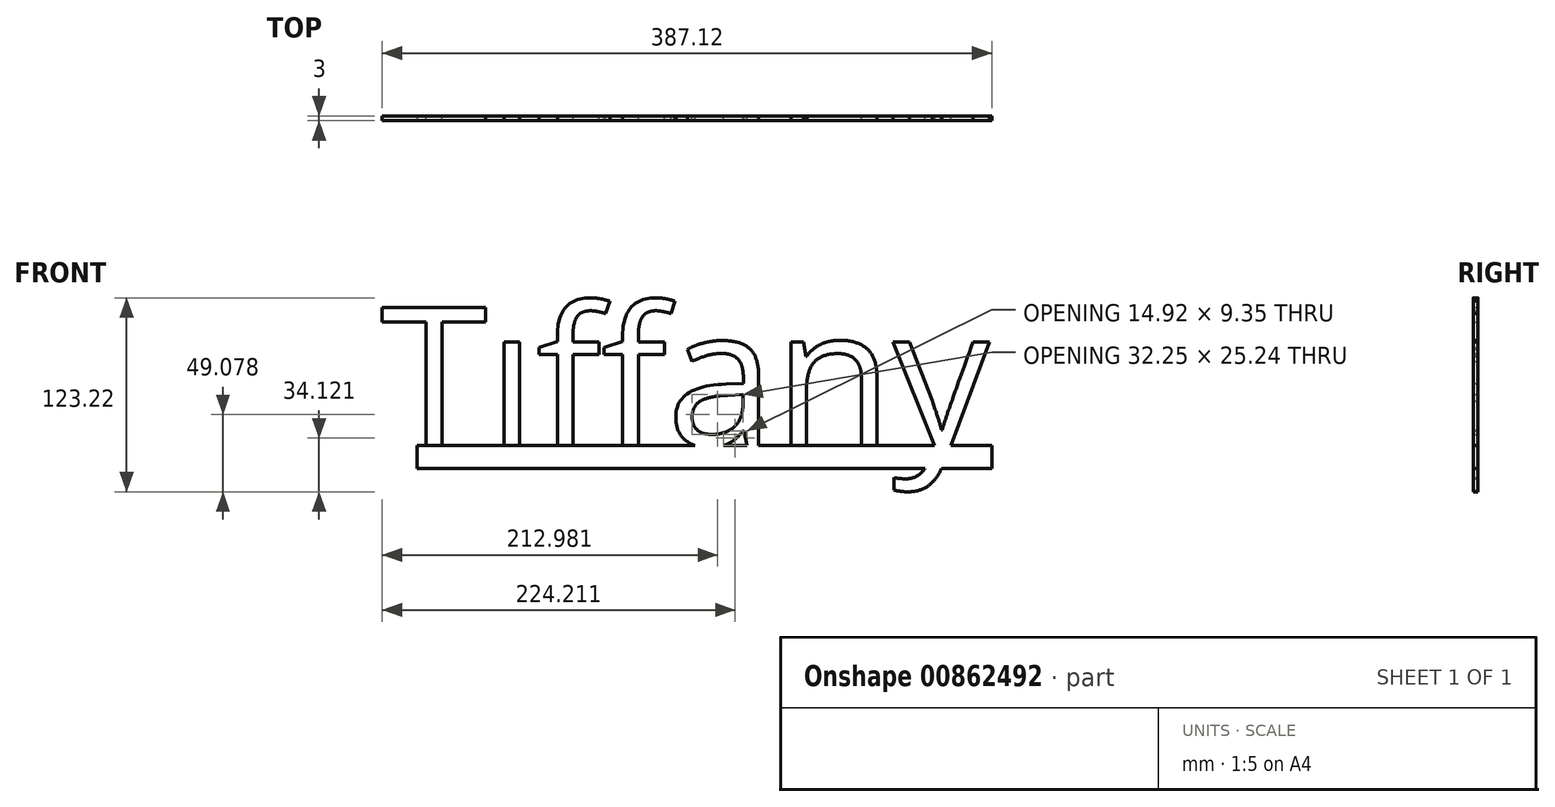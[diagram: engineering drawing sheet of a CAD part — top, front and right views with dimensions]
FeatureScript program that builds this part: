
annotation { "Feature Type Name" : "Feature", "Feature Type Description" : "" }
export const myFeature = defineFeature(function(context is Context, id is Id, definition is map)
    precondition{}
    {
        {
            var Q0;
            Q0=qCreatedBy(makeId("Front.planeOp"),FACE);
            var sketch = newSketch(context, id + "F0", { "sketchPlane" : qUnion([Q0])});
            skText(sketch, "E0", { "text": "Tiffany", "fontName": "OpenSans-Regular.ttf"});
            const initialGuessF0  = {"E0": [-0.16767, -0.10411, 1, 0, 0.08824]};
            skSetInitialGuess(sketch, initialGuessF0);
            skSolve(sketch);
        }
        {
            var Q0;
            Q0 = qSketchRegion(id + "F0", true);
            extrude(context, id + "F1", {"entities" : qUnion([Q0]), "depth" : 3 * mm, "offsetDistance" : 25.4 * mm});
        }
        {
            var Q0;
            Q0=makeQuery(id+"F1.opExtrude","CAP_FACE",FACE,{"disambiguationData":[OSD([sQuery(id+"F0.wireOp",EDGE,"E0.sketch_text.stroke-0"),sQuery(id+"F0.wireOp",EDGE,"E0.sketch_text.stroke-1"),sQuery(id+"F0.wireOp",EDGE,"E0.sketch_text.stroke-2"),sQuery(id+"F0.wireOp",EDGE,"E0.sketch_text.stroke-3"),sQuery(id+"F0.wireOp",EDGE,"E0.sketch_text.stroke-4"),sQuery(id+"F0.wireOp",EDGE,"E0.sketch_text.stroke-5"),sQuery(id+"F0.wireOp",EDGE,"E0.sketch_text.stroke-6"),sQuery(id+"F0.wireOp",EDGE,"E0.sketch_text.stroke-7")])],"isStart":false});
            var sketch = newSketch(context, id + "F2", { "sketchPlane" : qUnion([Q0])});
            skLineSegment(sketch, "E1.bottom", {"start": v(-144.5, -104.11) * mm, "end": v(220.52, -104.11) * mm});
            skLineSegment(sketch, "E1.top", {"start": v(-144.5, -118.7) * mm, "end": v(220.52, -118.7) * mm});
            skLineSegment(sketch, "E1.left", {"start": v(-144.5, -104.11) * mm, "end": v(-144.5, -118.7) * mm});
            skLineSegment(sketch, "E1.right", {"start": v(220.52, -104.11) * mm, "end": v(220.52, -118.7) * mm});
            skSolve(sketch);
        }
        {
            var Q0;
            Q0 = qSketchRegion(id + "F2", true);
            extrude(context, id + "F3", {"entities" : qUnion([Q0]), "operationType" : NewBodyOperationType.ADD, "oppositeDirection" : true, "depth" : 3 * mm, "offsetDistance" : 25.4 * mm});
        }
        {
            var Q0;
            Q0=makeQuery(id+"F1.opExtrude","SWEPT_BODY",BODY,{"disambiguationData":[OSD([sQuery(id+"F0.wireOp",EDGE,"E0.sketch_text.stroke-12"),sQuery(id+"F0.wireOp",EDGE,"E0.sketch_text.stroke-13"),sQuery(id+"F0.wireOp",EDGE,"E0.sketch_text.stroke-14"),sQuery(id+"F0.wireOp",EDGE,"E0.sketch_text.stroke-15"),sQuery(id+"F0.wireOp",EDGE,"E0.sketch_text.stroke-16"),sQuery(id+"F0.wireOp",EDGE,"E0.sketch_text.stroke-17"),sQuery(id+"F0.wireOp",EDGE,"E0.sketch_text.stroke-18"),sQuery(id+"F0.wireOp",EDGE,"E0.sketch_text.stroke-19")])]});
            deleteBodies(context, id + "F4", {"entities" : qUnion([Q0])});
        }
    });
